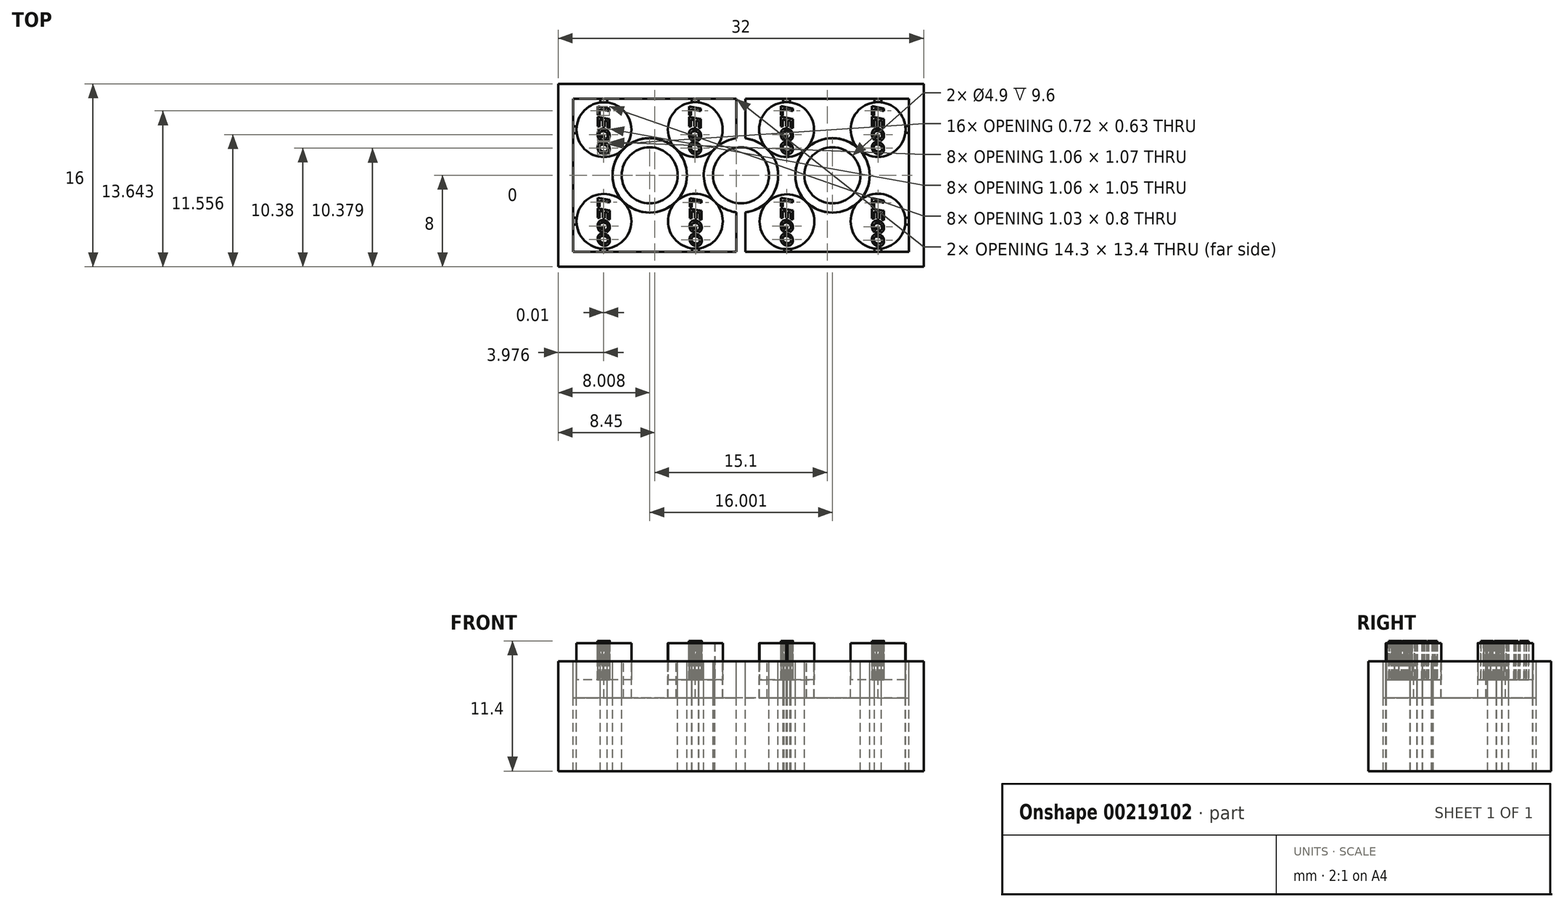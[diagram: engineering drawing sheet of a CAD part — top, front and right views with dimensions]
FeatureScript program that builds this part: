
annotation { "Feature Type Name" : "Feature", "Feature Type Description" : "" }
export const myFeature = defineFeature(function(context is Context, id is Id, definition is map)
    precondition{}
    {
        {
            var Q0;
            Q0=qCreatedBy(makeId("Top.planeOp"),FACE);
            var sketch = newSketch(context, id + "F0", { "sketchPlane" : qUnion([Q0])});
            skLineSegment(sketch, "E0.bottom", {"start": v(-16, 8) * mm, "end": v(16, 8) * mm});
            skLineSegment(sketch, "E0.top", {"start": v(-16, -8) * mm, "end": v(16, -8) * mm});
            skLineSegment(sketch, "E0.left", {"start": v(-16, 8) * mm, "end": v(-16, -8) * mm});
            skLineSegment(sketch, "E0.right", {"start": v(16, 8) * mm, "end": v(16, -8) * mm});
            skCircle(sketch, "E1", {"center": v(-12, 4) * mm, "radius": 2.4 * mm});
            skCircle(sketch, "E2", {"center": v(-4, 4) * mm, "radius": 2.4 * mm});
            skCircle(sketch, "E3", {"center": v(4, 4) * mm, "radius": 2.4 * mm});
            skCircle(sketch, "E4", {"center": v(12, 4.01) * mm, "radius": 2.4 * mm});
            skCircle(sketch, "E5", {"center": v(-12, -4.02) * mm, "radius": 2.4 * mm});
            skCircle(sketch, "E6", {"center": v(-3.99, -4.01) * mm, "radius": 2.4 * mm});
            skCircle(sketch, "E7", {"center": v(4.03, -4.05) * mm, "radius": 2.4 * mm});
            skCircle(sketch, "E8", {"center": v(12, -4.02) * mm, "radius": 2.4 * mm});
            skCircle(sketch, "E9", {"center": v(-8, 0) * mm, "radius": 3.26 * mm});
            skCircle(sketch, "E10", {"center": v(8, 0) * mm, "radius": 3.26 * mm});
            skLineSegment(sketch, "E11.0", {"start": v(-14.7, 6.7) * mm, "end": v(14.7, 6.7) * mm});
            skLineSegment(sketch, "E11.1", {"start": v(-14.7, 6.7) * mm, "end": v(-14.7, -6.7) * mm});
            skLineSegment(sketch, "E11.2", {"start": v(-14.7, -6.7) * mm, "end": v(14.7, -6.7) * mm});
            skLineSegment(sketch, "E11.3", {"start": v(14.7, 6.7) * mm, "end": v(14.7, -6.7) * mm});
            skCircle(sketch, "E12", {"center": v(0, 0) * mm, "radius": 3.26 * mm});
            skLineSegment(sketch, "E13", {"start": v(0.4, -6.7) * mm, "end": v(0.4, -3.23) * mm});
            skLineSegment(sketch, "E14", {"start": v(-0.4, -6.7) * mm, "end": v(-0.4, -3.23) * mm});
            skLineSegment(sketch, "E15.MirrorCS", {"start": v(-0.4, 6.7) * mm, "end": v(-0.4, 3.23) * mm});
            skLineSegment(sketch, "E16.MirrorCS", {"start": v(0.4, 6.7) * mm, "end": v(0.4, 3.23) * mm});
            skCircle(sketch, "E17", {"center": v(-8, 0) * mm, "radius": 2.45 * mm});
            skCircle(sketch, "E18", {"center": v(0, 0) * mm, "radius": 2.45 * mm});
            skCircle(sketch, "E19", {"center": v(8, 0) * mm, "radius": 2.45 * mm});
            skText(sketch, "E20", { "text": "LEGO", "fontName": "Arimo-BoldItalic.ttf"});
            skLineSegment(sketch, "E21", {"start": v(-12, -6.42) * mm, "end": v(-11.7, -6.42) * mm});
            skLineSegment(sketch, "E22", {"start": v(-11.7, -6.42) * mm, "end": v(-11.7, -6.7) * mm});
            skLineSegment(sketch, "E23", {"start": v(-12, -6.42) * mm, "end": v(-12.3, -6.42) * mm});
            skLineSegment(sketch, "E24", {"start": v(-12.3, -6.42) * mm, "end": v(-12.3, -6.7) * mm});
            skLineSegment(sketch, "E25", {"start": v(-14.4, -4.02) * mm, "end": v(-14.4, -3.72) * mm});
            skLineSegment(sketch, "E26", {"start": v(-14.4, -4.02) * mm, "end": v(-14.4, -4.32) * mm});
            skLineSegment(sketch, "E27", {"start": v(-14.4, -4.32) * mm, "end": v(-14.7, -4.32) * mm});
            skLineSegment(sketch, "E28", {"start": v(-14.4, -3.72) * mm, "end": v(-14.7, -3.72) * mm});
            skLineSegment(sketch, "E29", {"start": v(-14.4, 4) * mm, "end": v(-14.4, 4.3) * mm});
            skLineSegment(sketch, "E30", {"start": v(-14.4, 4) * mm, "end": v(-14.4, 3.7) * mm});
            skLineSegment(sketch, "E31", {"start": v(-14.4, 4.3) * mm, "end": v(-14.7, 4.3) * mm});
            skLineSegment(sketch, "E32", {"start": v(-14.4, 3.7) * mm, "end": v(-14.7, 3.7) * mm});
            skLineSegment(sketch, "E33", {"start": v(-12, 6.4) * mm, "end": v(-11.7, 6.4) * mm});
            skLineSegment(sketch, "E34", {"start": v(-12, 6.4) * mm, "end": v(-12.3, 6.4) * mm});
            skLineSegment(sketch, "E35", {"start": v(-11.7, 6.4) * mm, "end": v(-11.7, 6.7) * mm});
            skLineSegment(sketch, "E36", {"start": v(-12.3, 6.4) * mm, "end": v(-12.3, 6.7) * mm});
            skLineSegment(sketch, "E37", {"start": v(-4, 6.4) * mm, "end": v(-3.7, 6.4) * mm});
            skLineSegment(sketch, "E38", {"start": v(-4, 6.4) * mm, "end": v(-4.3, 6.4) * mm});
            skLineSegment(sketch, "E39", {"start": v(-4.3, 6.4) * mm, "end": v(-4.3, 6.7) * mm});
            skLineSegment(sketch, "E40", {"start": v(-3.7, 6.4) * mm, "end": v(-3.7, 6.7) * mm});
            skLineSegment(sketch, "E41", {"start": v(4.07, -6.45) * mm, "end": v(4.37, -6.45) * mm});
            skLineSegment(sketch, "E42", {"start": v(4.07, -6.45) * mm, "end": v(3.77, -6.45) * mm});
            skLineSegment(sketch, "E43", {"start": v(4.37, -6.45) * mm, "end": v(4.37, -6.7) * mm});
            skLineSegment(sketch, "E44", {"start": v(3.77, -6.45) * mm, "end": v(3.77, -6.7) * mm});
            skLineSegment(sketch, "E45", {"start": v(4, 6.4) * mm, "end": v(4.3, 6.4) * mm});
            skLineSegment(sketch, "E46", {"start": v(4, 6.4) * mm, "end": v(3.7, 6.4) * mm});
            skLineSegment(sketch, "E47", {"start": v(3.7, 6.4) * mm, "end": v(3.7, 6.7) * mm});
            skLineSegment(sketch, "E48", {"start": v(4.3, 6.4) * mm, "end": v(4.3, 6.7) * mm});
            skLineSegment(sketch, "E49", {"start": v(14.4, -4.02) * mm, "end": v(14.4, -4.32) * mm});
            skLineSegment(sketch, "E50", {"start": v(14.4, -3.72) * mm, "end": v(14.7, -3.72) * mm});
            skLineSegment(sketch, "E51", {"start": v(14.4, -4.32) * mm, "end": v(14.7, -4.32) * mm});
            skLineSegment(sketch, "E52", {"start": v(12, 6.41) * mm, "end": v(12.3, 6.41) * mm});
            skLineSegment(sketch, "E53", {"start": v(12, 6.41) * mm, "end": v(11.7, 6.41) * mm});
            skLineSegment(sketch, "E54", {"start": v(11.7, 6.41) * mm, "end": v(11.7, 6.7) * mm});
            skLineSegment(sketch, "E55", {"start": v(12.3, 6.41) * mm, "end": v(12.3, 6.7) * mm});
            skLineSegment(sketch, "E56", {"start": v(14.4, 4.01) * mm, "end": v(14.4, 4.31) * mm});
            skLineSegment(sketch, "E57", {"start": v(14.4, 4.01) * mm, "end": v(14.4, 3.71) * mm});
            skLineSegment(sketch, "E58", {"start": v(14.4, 3.71) * mm, "end": v(14.7, 3.71) * mm});
            skLineSegment(sketch, "E59", {"start": v(14.4, 4.31) * mm, "end": v(14.7, 4.31) * mm});
            skText(sketch, "E60", { "text": "LEGO", "fontName": "Arimo-BoldItalic.ttf"});
            skText(sketch, "E61", { "text": "LEGO", "fontName": "Arimo-BoldItalic.ttf"});
            skText(sketch, "E62", { "text": "LEGO", "fontName": "Arimo-BoldItalic.ttf"});
            skText(sketch, "E63", { "text": "LEGO", "fontName": "Arimo-BoldItalic.ttf"});
            skText(sketch, "E64", { "text": "LEGO", "fontName": "Arimo-BoldItalic.ttf"});
            skText(sketch, "E65", { "text": "LEGO", "fontName": "Arimo-BoldItalic.ttf"});
            skText(sketch, "E66", { "text": "LEGO", "fontName": "Arimo-BoldItalic.ttf"});
            skLineSegment(sketch, "E67.bottom", {"start": v(14.7, 6.7) * mm, "end": v(-14.7, 6.7) * mm});
            skLineSegment(sketch, "E67.top", {"start": v(14.7, -6.7) * mm, "end": v(-14.7, -6.7) * mm});
            skLineSegment(sketch, "E68", {"start": v(14.4, -3.72) * mm, "end": v(14.4, -4.02) * mm});
            skLineSegment(sketch, "E69", {"start": v(12, -6.42) * mm, "end": v(12.3, -6.42) * mm});
            skLineSegment(sketch, "E70", {"start": v(12, -6.42) * mm, "end": v(11.7, -6.42) * mm});
            skLineSegment(sketch, "E71", {"start": v(11.7, -6.42) * mm, "end": v(11.7, -6.7) * mm});
            skLineSegment(sketch, "E72", {"start": v(12.3, -6.42) * mm, "end": v(12.3, -6.7) * mm});
            skLineSegment(sketch, "E73", {"start": v(-3.99, -6.41) * mm, "end": v(-3.69, -6.41) * mm});
            skLineSegment(sketch, "E74", {"start": v(-3.99, -6.41) * mm, "end": v(-4.29, -6.41) * mm});
            skLineSegment(sketch, "E75", {"start": v(-4.29, -6.41) * mm, "end": v(-4.29, -6.7) * mm});
            skLineSegment(sketch, "E76", {"start": v(-3.69, -6.41) * mm, "end": v(-3.69, -6.7) * mm});
            skLineSegment(sketch, "E77", {"start": v(2.3, 2.3) * mm, "end": v(2.3, 2.3) * mm});
            skLineSegment(sketch, "E78", {"start": v(5.7, 2.33) * mm, "end": v(5.72, 2.32) * mm});
            skLineSegment(sketch, "E79", {"start": v(5.74, -2.34) * mm, "end": v(5.72, -2.35) * mm});
            skLineSegment(sketch, "E80", {"start": v(10.29, 2.34) * mm, "end": v(10.28, 2.33) * mm});
            skLineSegment(sketch, "E81", {"start": v(-10.3, -2.34) * mm, "end": v(-10.28, -2.32) * mm});
            skLineSegment(sketch, "E82", {"start": v(-5.7, 2.3) * mm, "end": v(-5.7, 2.3) * mm});
            const initialGuessF0  = {"E20": [-0.00454, 0.00607, 0, -1, 0.00108], "E60": [-0.01254, 0.00607, 0, -1, 0.00108], "E61": [0.0035, 0.00608, 0, -1, 0.00108], "E62": [0.01148, 0.00608, 0, -1, 0.00108], "E63": [-0.00448, -0.00196, 0, -1, 0.00108], "E64": [-0.01253, -0.00193, 0, -1, 0.00108], "E65": [0.0035, -0.00193, 0, -1, 0.00108], "E66": [0.01148, -0.00198, 0, -1, 0.00108]};
            skSetInitialGuess(sketch, initialGuessF0);
            skSolve(sketch);
        }
        {
            var Q0;
            Q0=makeQuery(id+"F0.imprint","IMPRINT",FACE,{"disambiguationData":[TD([[makeQuery(id+"F0.imprint","IMPRINT",EDGE,{"derivedFrom":sQuery(id+"F0.wireOp",EDGE,"E0.bottom")}),-1.0]])]});
            var Q1;
            Q1=makeQuery(id+"F0.imprint","IMPRINT",FACE,{"disambiguationData":[TD([[makeQuery(id+"F0.imprint","IMPRINT",EDGE,{"derivedFrom":sQuery(id+"F0.wireOp",EDGE,"E9")}),1.0]])]});
            var Q2;
            Q2=makeQuery(id+"F0.imprint","IMPRINT",FACE,{"disambiguationData":[TD([[makeQuery(id+"F0.imprint","IMPRINT",EDGE,{"derivedFrom":sQuery(id+"F0.wireOp",EDGE,"E18")}),-1.0]])]});
            var Q3;
            {var subQ0=sQuery(id+"F0.wireOp",EDGE,"E15.MirrorCS");Q3=makeQuery(id+"F0.imprint","IMPRINT",FACE,{"disambiguationData":[TD([[makeQuery(id+"F0.imprint","IMPRINT",EDGE,{"derivedFrom":subQ0}),1.0]])]});}
            var Q4;
            {var subQ0=sQuery(id+"F0.wireOp",EDGE,"E13");Q4=makeQuery(id+"F0.imprint","IMPRINT",FACE,{"disambiguationData":[TD([[makeQuery(id+"F0.imprint","IMPRINT",EDGE,{"derivedFrom":subQ0}),1.0]])]});}
            var Q5;
            Q5=makeQuery(id+"F0.imprint","IMPRINT",FACE,{"disambiguationData":[TD([[makeQuery(id+"F0.imprint","IMPRINT",EDGE,{"derivedFrom":sQuery(id+"F0.wireOp",EDGE,"E10")}),1.0]])]});
            extrude(context, id + "F1", {"entities" : qUnion([Q0, Q1, Q2, Q3, Q4, Q5]), "oppositeDirection" : true, "depth" : 9.6 * mm});
        }
        {
            var Q0;
            Q0=makeQuery(id+"F0.imprint","IMPRINT",FACE,{"disambiguationData":[TD([[makeQuery(id+"F0.imprint","IMPRINT",EDGE,{"derivedFrom":sQuery(id+"F0.wireOp",EDGE,"E65.sketch_text.stroke-0")}),1.0]])]});
            var Q1;
            Q1=makeQuery(id+"F0.imprint","IMPRINT",FACE,{"disambiguationData":[TD([[makeQuery(id+"F0.imprint","IMPRINT",EDGE,{"derivedFrom":sQuery(id+"F0.wireOp",EDGE,"E65.sketch_text.stroke-53")}),1.0]])]});
            var Q2;
            Q2=makeQuery(id+"F0.imprint","IMPRINT",FACE,{"disambiguationData":[TD([[makeQuery(id+"F0.imprint","IMPRINT",EDGE,{"derivedFrom":sQuery(id+"F0.wireOp",EDGE,"E66.sketch_text.stroke-53")}),1.0]])]});
            var Q3;
            Q3=makeQuery(id+"F0.imprint","IMPRINT",FACE,{"disambiguationData":[TD([[makeQuery(id+"F0.imprint","IMPRINT",EDGE,{"derivedFrom":sQuery(id+"F0.wireOp",EDGE,"E66.sketch_text.stroke-0")}),1.0]])]});
            var Q4;
            Q4=makeQuery(id+"F0.imprint","IMPRINT",FACE,{"disambiguationData":[TD([[makeQuery(id+"F0.imprint","IMPRINT",EDGE,{"derivedFrom":sQuery(id+"F0.wireOp",EDGE,"E63.sketch_text.stroke-0")}),1.0]])]});
            var Q5;
            Q5=makeQuery(id+"F0.imprint","IMPRINT",FACE,{"disambiguationData":[TD([[makeQuery(id+"F0.imprint","IMPRINT",EDGE,{"derivedFrom":sQuery(id+"F0.wireOp",EDGE,"E63.sketch_text.stroke-53")}),1.0]])]});
            var Q6;
            Q6=makeQuery(id+"F0.imprint","IMPRINT",FACE,{"disambiguationData":[TD([[makeQuery(id+"F0.imprint","IMPRINT",EDGE,{"derivedFrom":sQuery(id+"F0.wireOp",EDGE,"E64.sketch_text.stroke-0")}),1.0]])]});
            var Q7;
            Q7=makeQuery(id+"F0.imprint","IMPRINT",FACE,{"disambiguationData":[TD([[makeQuery(id+"F0.imprint","IMPRINT",EDGE,{"derivedFrom":sQuery(id+"F0.wireOp",EDGE,"E64.sketch_text.stroke-53")}),1.0]])]});
            var Q8;
            Q8=makeQuery(id+"F0.imprint","IMPRINT",FACE,{"disambiguationData":[TD([[makeQuery(id+"F0.imprint","IMPRINT",EDGE,{"derivedFrom":sQuery(id+"F0.wireOp",EDGE,"E60.sketch_text.stroke-0")}),1.0]])]});
            var Q9;
            Q9=makeQuery(id+"F0.imprint","IMPRINT",FACE,{"disambiguationData":[TD([[makeQuery(id+"F0.imprint","IMPRINT",EDGE,{"derivedFrom":sQuery(id+"F0.wireOp",EDGE,"E60.sketch_text.stroke-53")}),1.0]])]});
            var Q10;
            Q10=makeQuery(id+"F0.imprint","IMPRINT",FACE,{"disambiguationData":[TD([[makeQuery(id+"F0.imprint","IMPRINT",EDGE,{"derivedFrom":sQuery(id+"F0.wireOp",EDGE,"E20.sketch_text.stroke-53")}),1.0]])]});
            var Q11;
            Q11=makeQuery(id+"F0.imprint","IMPRINT",FACE,{"disambiguationData":[TD([[makeQuery(id+"F0.imprint","IMPRINT",EDGE,{"derivedFrom":sQuery(id+"F0.wireOp",EDGE,"E2")}),1.0]])]});
            var Q12;
            Q12=makeQuery(id+"F0.imprint","IMPRINT",FACE,{"disambiguationData":[TD([[makeQuery(id+"F0.imprint","IMPRINT",EDGE,{"derivedFrom":sQuery(id+"F0.wireOp",EDGE,"E61.sketch_text.stroke-53")}),1.0]])]});
            var Q13;
            Q13=makeQuery(id+"F0.imprint","IMPRINT",FACE,{"disambiguationData":[TD([[makeQuery(id+"F0.imprint","IMPRINT",EDGE,{"derivedFrom":sQuery(id+"F0.wireOp",EDGE,"E3")}),1.0]])]});
            var Q14;
            Q14=makeQuery(id+"F0.imprint","IMPRINT",FACE,{"disambiguationData":[TD([[makeQuery(id+"F0.imprint","IMPRINT",EDGE,{"derivedFrom":sQuery(id+"F0.wireOp",EDGE,"E62.sketch_text.stroke-53")}),1.0]])]});
            var Q15;
            Q15=makeQuery(id+"F0.imprint","IMPRINT",FACE,{"disambiguationData":[TD([[makeQuery(id+"F0.imprint","IMPRINT",EDGE,{"derivedFrom":sQuery(id+"F0.wireOp",EDGE,"E62.sketch_text.stroke-0")}),1.0]])]});
            extrude(context, id + "F2", {"entities" : qUnion([Q0, Q1, Q2, Q3, Q4, Q5, Q6, Q7, Q8, Q9, Q10, Q11, Q12, Q13, Q14, Q15]), "endBound" : BoundingType.SYMMETRIC, "depth" : 3.2 * mm});
        }
        {
            var Q0;
            Q0=makeQuery(id+"F0.imprint","IMPRINT",FACE,{"disambiguationData":[TD([[makeQuery(id+"F0.imprint","IMPRINT",EDGE,{"derivedFrom":sQuery(id+"F0.wireOp",EDGE,"E20.sketch_text.stroke-42")}),-1.0]])]});
            var Q1;
            Q1=makeQuery(id+"F0.imprint","IMPRINT",FACE,{"disambiguationData":[TD([[makeQuery(id+"F0.imprint","IMPRINT",EDGE,{"derivedFrom":sQuery(id+"F0.wireOp",EDGE,"E20.sketch_text.stroke-18")}),-1.0]])]});
            var Q2;
            Q2=makeQuery(id+"F0.imprint","IMPRINT",FACE,{"disambiguationData":[TD([[makeQuery(id+"F0.imprint","IMPRINT",EDGE,{"derivedFrom":sQuery(id+"F0.wireOp",EDGE,"E20.sketch_text.stroke-6")}),-1.0]])]});
            var Q3;
            Q3=makeQuery(id+"F0.imprint","IMPRINT",FACE,{"disambiguationData":[TD([[makeQuery(id+"F0.imprint","IMPRINT",EDGE,{"derivedFrom":sQuery(id+"F0.wireOp",EDGE,"E20.sketch_text.stroke-0")}),-1.0]])]});
            var Q4;
            Q4=makeQuery(id+"F0.imprint","IMPRINT",FACE,{"disambiguationData":[TD([[makeQuery(id+"F0.imprint","IMPRINT",EDGE,{"derivedFrom":sQuery(id+"F0.wireOp",EDGE,"E60.sketch_text.stroke-0")}),-1.0]])]});
            var Q5;
            Q5=makeQuery(id+"F0.imprint","IMPRINT",FACE,{"disambiguationData":[TD([[makeQuery(id+"F0.imprint","IMPRINT",EDGE,{"derivedFrom":sQuery(id+"F0.wireOp",EDGE,"E60.sketch_text.stroke-6")}),-1.0]])]});
            var Q6;
            Q6=makeQuery(id+"F0.imprint","IMPRINT",FACE,{"disambiguationData":[TD([[makeQuery(id+"F0.imprint","IMPRINT",EDGE,{"derivedFrom":sQuery(id+"F0.wireOp",EDGE,"E60.sketch_text.stroke-18")}),-1.0]])]});
            var Q7;
            Q7=makeQuery(id+"F0.imprint","IMPRINT",FACE,{"disambiguationData":[TD([[makeQuery(id+"F0.imprint","IMPRINT",EDGE,{"derivedFrom":sQuery(id+"F0.wireOp",EDGE,"E60.sketch_text.stroke-42")}),-1.0]])]});
            var Q8;
            Q8=makeQuery(id+"F0.imprint","IMPRINT",FACE,{"disambiguationData":[TD([[makeQuery(id+"F0.imprint","IMPRINT",EDGE,{"derivedFrom":sQuery(id+"F0.wireOp",EDGE,"E64.sketch_text.stroke-0")}),-1.0]])]});
            var Q9;
            Q9=makeQuery(id+"F0.imprint","IMPRINT",FACE,{"disambiguationData":[TD([[makeQuery(id+"F0.imprint","IMPRINT",EDGE,{"derivedFrom":sQuery(id+"F0.wireOp",EDGE,"E64.sketch_text.stroke-6")}),-1.0]])]});
            var Q10;
            Q10=makeQuery(id+"F0.imprint","IMPRINT",FACE,{"disambiguationData":[TD([[makeQuery(id+"F0.imprint","IMPRINT",EDGE,{"derivedFrom":sQuery(id+"F0.wireOp",EDGE,"E64.sketch_text.stroke-18")}),-1.0]])]});
            var Q11;
            Q11=makeQuery(id+"F0.imprint","IMPRINT",FACE,{"disambiguationData":[TD([[makeQuery(id+"F0.imprint","IMPRINT",EDGE,{"derivedFrom":sQuery(id+"F0.wireOp",EDGE,"E64.sketch_text.stroke-42")}),-1.0]])]});
            var Q12;
            Q12=makeQuery(id+"F0.imprint","IMPRINT",FACE,{"disambiguationData":[TD([[makeQuery(id+"F0.imprint","IMPRINT",EDGE,{"derivedFrom":sQuery(id+"F0.wireOp",EDGE,"E63.sketch_text.stroke-42")}),-1.0]])]});
            var Q13;
            Q13=makeQuery(id+"F0.imprint","IMPRINT",FACE,{"disambiguationData":[TD([[makeQuery(id+"F0.imprint","IMPRINT",EDGE,{"derivedFrom":sQuery(id+"F0.wireOp",EDGE,"E63.sketch_text.stroke-18")}),-1.0]])]});
            var Q14;
            Q14=makeQuery(id+"F0.imprint","IMPRINT",FACE,{"disambiguationData":[TD([[makeQuery(id+"F0.imprint","IMPRINT",EDGE,{"derivedFrom":sQuery(id+"F0.wireOp",EDGE,"E63.sketch_text.stroke-6")}),-1.0]])]});
            var Q15;
            Q15=makeQuery(id+"F0.imprint","IMPRINT",FACE,{"disambiguationData":[TD([[makeQuery(id+"F0.imprint","IMPRINT",EDGE,{"derivedFrom":sQuery(id+"F0.wireOp",EDGE,"E63.sketch_text.stroke-0")}),-1.0]])]});
            var Q16;
            Q16=makeQuery(id+"F0.imprint","IMPRINT",FACE,{"disambiguationData":[TD([[makeQuery(id+"F0.imprint","IMPRINT",EDGE,{"derivedFrom":sQuery(id+"F0.wireOp",EDGE,"E65.sketch_text.stroke-18")}),-1.0]])]});
            var Q17;
            Q17=makeQuery(id+"F0.imprint","IMPRINT",FACE,{"disambiguationData":[TD([[makeQuery(id+"F0.imprint","IMPRINT",EDGE,{"derivedFrom":sQuery(id+"F0.wireOp",EDGE,"E65.sketch_text.stroke-42")}),-1.0]])]});
            var Q18;
            Q18=makeQuery(id+"F0.imprint","IMPRINT",FACE,{"disambiguationData":[TD([[makeQuery(id+"F0.imprint","IMPRINT",EDGE,{"derivedFrom":sQuery(id+"F0.wireOp",EDGE,"E65.sketch_text.stroke-6")}),-1.0]])]});
            var Q19;
            Q19=makeQuery(id+"F0.imprint","IMPRINT",FACE,{"disambiguationData":[TD([[makeQuery(id+"F0.imprint","IMPRINT",EDGE,{"derivedFrom":sQuery(id+"F0.wireOp",EDGE,"E65.sketch_text.stroke-0")}),-1.0]])]});
            var Q20;
            Q20=makeQuery(id+"F0.imprint","IMPRINT",FACE,{"disambiguationData":[TD([[makeQuery(id+"F0.imprint","IMPRINT",EDGE,{"derivedFrom":sQuery(id+"F0.wireOp",EDGE,"E61.sketch_text.stroke-42")}),-1.0]])]});
            var Q21;
            Q21=makeQuery(id+"F0.imprint","IMPRINT",FACE,{"disambiguationData":[TD([[makeQuery(id+"F0.imprint","IMPRINT",EDGE,{"derivedFrom":sQuery(id+"F0.wireOp",EDGE,"E61.sketch_text.stroke-18")}),-1.0]])]});
            var Q22;
            Q22=makeQuery(id+"F0.imprint","IMPRINT",FACE,{"disambiguationData":[TD([[makeQuery(id+"F0.imprint","IMPRINT",EDGE,{"derivedFrom":sQuery(id+"F0.wireOp",EDGE,"E61.sketch_text.stroke-6")}),-1.0]])]});
            var Q23;
            Q23=makeQuery(id+"F0.imprint","IMPRINT",FACE,{"disambiguationData":[TD([[makeQuery(id+"F0.imprint","IMPRINT",EDGE,{"derivedFrom":sQuery(id+"F0.wireOp",EDGE,"E61.sketch_text.stroke-0")}),-1.0]])]});
            var Q24;
            Q24=makeQuery(id+"F0.imprint","IMPRINT",FACE,{"disambiguationData":[TD([[makeQuery(id+"F0.imprint","IMPRINT",EDGE,{"derivedFrom":sQuery(id+"F0.wireOp",EDGE,"E62.sketch_text.stroke-0")}),-1.0]])]});
            var Q25;
            Q25=makeQuery(id+"F0.imprint","IMPRINT",FACE,{"disambiguationData":[TD([[makeQuery(id+"F0.imprint","IMPRINT",EDGE,{"derivedFrom":sQuery(id+"F0.wireOp",EDGE,"E62.sketch_text.stroke-6")}),-1.0]])]});
            var Q26;
            Q26=makeQuery(id+"F0.imprint","IMPRINT",FACE,{"disambiguationData":[TD([[makeQuery(id+"F0.imprint","IMPRINT",EDGE,{"derivedFrom":sQuery(id+"F0.wireOp",EDGE,"E62.sketch_text.stroke-18")}),-1.0]])]});
            var Q27;
            Q27=makeQuery(id+"F0.imprint","IMPRINT",FACE,{"disambiguationData":[TD([[makeQuery(id+"F0.imprint","IMPRINT",EDGE,{"derivedFrom":sQuery(id+"F0.wireOp",EDGE,"E62.sketch_text.stroke-42")}),-1.0]])]});
            var Q28;
            Q28=makeQuery(id+"F0.imprint","IMPRINT",FACE,{"disambiguationData":[TD([[makeQuery(id+"F0.imprint","IMPRINT",EDGE,{"derivedFrom":sQuery(id+"F0.wireOp",EDGE,"E66.sketch_text.stroke-0")}),-1.0]])]});
            var Q29;
            Q29=makeQuery(id+"F0.imprint","IMPRINT",FACE,{"disambiguationData":[TD([[makeQuery(id+"F0.imprint","IMPRINT",EDGE,{"derivedFrom":sQuery(id+"F0.wireOp",EDGE,"E66.sketch_text.stroke-6")}),-1.0]])]});
            var Q30;
            Q30=makeQuery(id+"F0.imprint","IMPRINT",FACE,{"disambiguationData":[TD([[makeQuery(id+"F0.imprint","IMPRINT",EDGE,{"derivedFrom":sQuery(id+"F0.wireOp",EDGE,"E66.sketch_text.stroke-18")}),-1.0]])]});
            var Q31;
            Q31=makeQuery(id+"F0.imprint","IMPRINT",FACE,{"disambiguationData":[TD([[makeQuery(id+"F0.imprint","IMPRINT",EDGE,{"derivedFrom":sQuery(id+"F0.wireOp",EDGE,"E66.sketch_text.stroke-42")}),-1.0]])]});
            extrude(context, id + "F3", {"entities" : qUnion([Q0, Q1, Q2, Q3, Q4, Q5, Q6, Q7, Q8, Q9, Q10, Q11, Q12, Q13, Q14, Q15, Q16, Q17, Q18, Q19, Q20, Q21, Q22, Q23, Q24, Q25, Q26, Q27, Q28, Q29, Q30, Q31]), "depth" : 1.8 * mm});
        }
        {
            var Q0;
            Q0=makeQuery(id+"F0.imprint","IMPRINT",FACE,{"disambiguationData":[TD([[makeQuery(id+"F0.imprint","IMPRINT",EDGE,{"derivedFrom":sQuery(id+"F0.wireOp",EDGE,"E18")}),1.0]])]});
            var Q1;
            Q1=makeQuery(id+"F0.imprint","IMPRINT",FACE,{"disambiguationData":[TD([[makeQuery(id+"F0.imprint","IMPRINT",EDGE,{"derivedFrom":sQuery(id+"F0.wireOp",EDGE,"E17")}),1.0]])]});
            var Q2;
            Q2=makeQuery(id+"F0.imprint","IMPRINT",FACE,{"disambiguationData":[TD([[makeQuery(id+"F0.imprint","IMPRINT",EDGE,{"derivedFrom":sQuery(id+"F0.wireOp",EDGE,"E19")}),1.0]])]});
            extrude(context, id + "F4", {"entities" : qUnion([Q0, Q1, Q2]), "oppositeDirection" : true, "depth" : 3.2 * mm});
        }
        {
            var Q0;
            {var subQ0=sQuery(id+"F0.wireOp",EDGE,"E45");Q0=makeQuery(id+"F0.imprint","IMPRINT",FACE,{"disambiguationData":[TD([[makeQuery(id+"F0.imprint","IMPRINT",EDGE,{"derivedFrom":subQ0}),-1.0]])]});}
            var Q1;
            {var subQ1=sQuery(id+"F0.wireOp",EDGE,"E16.MirrorCS");Q1=makeQuery(id+"F0.imprint","IMPRINT",FACE,{"disambiguationData":[TD([[makeQuery(id+"F0.imprint","IMPRINT",EDGE,{"derivedFrom":subQ1}),1.0]])]});}
            var Q2;
            {var subQ0=sQuery(id+"F0.wireOp",EDGE,"E52");Q2=makeQuery(id+"F0.imprint","IMPRINT",FACE,{"disambiguationData":[TD([[makeQuery(id+"F0.imprint","IMPRINT",EDGE,{"derivedFrom":subQ0}),-1.0]])]});}
            var Q3;
            {var subQ5=sQuery(id+"F0.wireOp",EDGE,"E41");Q3=makeQuery(id+"F0.imprint","IMPRINT",FACE,{"disambiguationData":[TD([[makeQuery(id+"F0.imprint","IMPRINT",EDGE,{"derivedFrom":subQ5}),1.0]])]});}
            var Q4;
            {var subQ5=sQuery(id+"F0.wireOp",EDGE,"E49");Q4=makeQuery(id+"F0.imprint","IMPRINT",FACE,{"disambiguationData":[TD([[makeQuery(id+"F0.imprint","IMPRINT",EDGE,{"derivedFrom":subQ5}),-1.0]])]});}
            extrude(context, id + "F5", {"entities" : qUnion([Q0, Q1, Q2, Q3, Q4]), "oppositeDirection" : true, "depth" : 3.2 * mm});
        }
        {
            var Q0;
            {var subQ2=sQuery(id+"F0.wireOp",EDGE,"E13");Q0=makeQuery(id+"F0.imprint","IMPRINT",FACE,{"disambiguationData":[TD([[makeQuery(id+"F0.imprint","IMPRINT",EDGE,{"derivedFrom":subQ2}),-1.0]])]});}
            extrude(context, id + "F6", {"entities" : qUnion([Q0]), "oppositeDirection" : true, "depth" : 3.2 * mm});
        }
        {
            var Q0;
            {var subQ1=sQuery(id+"F0.wireOp",EDGE,"E14");Q0=makeQuery(id+"F0.imprint","IMPRINT",FACE,{"disambiguationData":[TD([[makeQuery(id+"F0.imprint","IMPRINT",EDGE,{"derivedFrom":subQ1}),1.0]])]});}
            var Q1;
            {var subQ1=sQuery(id+"F0.wireOp",EDGE,"E29");Q1=makeQuery(id+"F0.imprint","IMPRINT",FACE,{"disambiguationData":[TD([[makeQuery(id+"F0.imprint","IMPRINT",EDGE,{"derivedFrom":subQ1}),-1.0]])]});}
            var Q2;
            {var subQ2=sQuery(id+"F0.wireOp",EDGE,"E23");Q2=makeQuery(id+"F0.imprint","IMPRINT",FACE,{"disambiguationData":[TD([[makeQuery(id+"F0.imprint","IMPRINT",EDGE,{"derivedFrom":subQ2}),-1.0]])]});}
            var Q3;
            {var subQ3=sQuery(id+"F0.wireOp",EDGE,"E15.MirrorCS");Q3=makeQuery(id+"F0.imprint","IMPRINT",FACE,{"disambiguationData":[TD([[makeQuery(id+"F0.imprint","IMPRINT",EDGE,{"derivedFrom":subQ3}),-1.0]])]});}
            extrude(context, id + "F7", {"entities" : qUnion([Q0, Q1, Q2, Q3]), "oppositeDirection" : true, "depth" : 3.2 * mm});
        }
        {
            var Q0;
            {var subQ9=sQuery(id+"F0.wireOp",EDGE,"E25");Q0=makeQuery(id+"F0.imprint","IMPRINT",FACE,{"disambiguationData":[TD([[makeQuery(id+"F0.imprint","IMPRINT",EDGE,{"derivedFrom":subQ9}),-1.0]])]});}
            extrude(context, id + "F8", {"entities" : qUnion([Q0]), "oppositeDirection" : true, "depth" : 3.2 * mm});
        }
        {
            var Q0;
            Q0=makeQuery(id+"F0.imprint","IMPRINT",FACE,{"disambiguationData":[TD([[makeQuery(id+"F0.imprint","IMPRINT",EDGE,{"derivedFrom":sQuery(id+"F0.wireOp",EDGE,"E52")}),1.0]])]});
            var Q1;
            Q1=makeQuery(id+"F0.imprint","IMPRINT",FACE,{"disambiguationData":[TD([[makeQuery(id+"F0.imprint","IMPRINT",EDGE,{"derivedFrom":sQuery(id+"F0.wireOp",EDGE,"E56")}),-1.0]])]});
            var Q2;
            {var subQ3=sQuery(id+"F0.wireOp",EDGE,"E49");Q2=makeQuery(id+"F0.imprint","IMPRINT",FACE,{"disambiguationData":[TD([[makeQuery(id+"F0.imprint","IMPRINT",EDGE,{"derivedFrom":subQ3}),1.0]])]});}
            var Q3;
            Q3=makeQuery(id+"F0.imprint","IMPRINT",FACE,{"disambiguationData":[TD([[makeQuery(id+"F0.imprint","IMPRINT",EDGE,{"derivedFrom":sQuery(id+"F0.wireOp",EDGE,"E69")}),-1.0]])]});
            var Q4;
            {var subQ6=sQuery(id+"F0.wireOp",EDGE,"E41");Q4=makeQuery(id+"F0.imprint","IMPRINT",FACE,{"disambiguationData":[TD([[makeQuery(id+"F0.imprint","IMPRINT",EDGE,{"derivedFrom":subQ6}),-1.0]])]});}
            var Q5;
            Q5=makeQuery(id+"F0.imprint","IMPRINT",FACE,{"disambiguationData":[TD([[makeQuery(id+"F0.imprint","IMPRINT",EDGE,{"derivedFrom":sQuery(id+"F0.wireOp",EDGE,"E45")}),1.0]])]});
            var Q6;
            Q6=makeQuery(id+"F0.imprint","IMPRINT",FACE,{"disambiguationData":[TD([[makeQuery(id+"F0.imprint","IMPRINT",EDGE,{"derivedFrom":sQuery(id+"F0.wireOp",EDGE,"E37")}),1.0]])]});
            var Q7;
            Q7=makeQuery(id+"F0.imprint","IMPRINT",FACE,{"disambiguationData":[TD([[makeQuery(id+"F0.imprint","IMPRINT",EDGE,{"derivedFrom":sQuery(id+"F0.wireOp",EDGE,"E73")}),-1.0]])]});
            var Q8;
            Q8=makeQuery(id+"F0.imprint","IMPRINT",FACE,{"disambiguationData":[TD([[makeQuery(id+"F0.imprint","IMPRINT",EDGE,{"derivedFrom":sQuery(id+"F0.wireOp",EDGE,"E21")}),-1.0]])]});
            var Q9;
            Q9=makeQuery(id+"F0.imprint","IMPRINT",FACE,{"disambiguationData":[TD([[makeQuery(id+"F0.imprint","IMPRINT",EDGE,{"derivedFrom":sQuery(id+"F0.wireOp",EDGE,"E25")}),1.0]])]});
            var Q10;
            Q10=makeQuery(id+"F0.imprint","IMPRINT",FACE,{"disambiguationData":[TD([[makeQuery(id+"F0.imprint","IMPRINT",EDGE,{"derivedFrom":sQuery(id+"F0.wireOp",EDGE,"E29")}),1.0]])]});
            var Q11;
            Q11=makeQuery(id+"F0.imprint","IMPRINT",FACE,{"disambiguationData":[TD([[makeQuery(id+"F0.imprint","IMPRINT",EDGE,{"derivedFrom":sQuery(id+"F0.wireOp",EDGE,"E33")}),1.0]])]});
            extrude(context, id + "F9", {"entities" : qUnion([Q0, Q1, Q2, Q3, Q4, Q5, Q6, Q7, Q8, Q9, Q10, Q11]), "oppositeDirection" : true, "depth" : 9.6 * mm});
        }
        {
            var Q0;
            Q0=makeQuery(id+"F0.imprint","IMPRINT",FACE,{"disambiguationData":[TD([[makeQuery(id+"F0.imprint","IMPRINT",EDGE,{"derivedFrom":sQuery(id+"F0.wireOp",EDGE,"E60.sketch_text.stroke-42")}),-1.0]])]});
            var Q1;
            Q1=makeQuery(id+"F0.imprint","IMPRINT",FACE,{"disambiguationData":[TD([[makeQuery(id+"F0.imprint","IMPRINT",EDGE,{"derivedFrom":sQuery(id+"F0.wireOp",EDGE,"E60.sketch_text.stroke-18")}),-1.0]])]});
            var Q2;
            Q2=makeQuery(id+"F0.imprint","IMPRINT",FACE,{"disambiguationData":[TD([[makeQuery(id+"F0.imprint","IMPRINT",EDGE,{"derivedFrom":sQuery(id+"F0.wireOp",EDGE,"E60.sketch_text.stroke-6")}),-1.0]])]});
            var Q3;
            Q3=makeQuery(id+"F0.imprint","IMPRINT",FACE,{"disambiguationData":[TD([[makeQuery(id+"F0.imprint","IMPRINT",EDGE,{"derivedFrom":sQuery(id+"F0.wireOp",EDGE,"E60.sketch_text.stroke-0")}),-1.0]])]});
            var Q4;
            Q4=makeQuery(id+"F0.imprint","IMPRINT",FACE,{"disambiguationData":[TD([[makeQuery(id+"F0.imprint","IMPRINT",EDGE,{"derivedFrom":sQuery(id+"F0.wireOp",EDGE,"E20.sketch_text.stroke-42")}),-1.0]])]});
            var Q5;
            Q5=makeQuery(id+"F0.imprint","IMPRINT",FACE,{"disambiguationData":[TD([[makeQuery(id+"F0.imprint","IMPRINT",EDGE,{"derivedFrom":sQuery(id+"F0.wireOp",EDGE,"E20.sketch_text.stroke-18")}),-1.0]])]});
            var Q6;
            Q6=makeQuery(id+"F0.imprint","IMPRINT",FACE,{"disambiguationData":[TD([[makeQuery(id+"F0.imprint","IMPRINT",EDGE,{"derivedFrom":sQuery(id+"F0.wireOp",EDGE,"E20.sketch_text.stroke-6")}),-1.0]])]});
            var Q7;
            Q7=makeQuery(id+"F0.imprint","IMPRINT",FACE,{"disambiguationData":[TD([[makeQuery(id+"F0.imprint","IMPRINT",EDGE,{"derivedFrom":sQuery(id+"F0.wireOp",EDGE,"E20.sketch_text.stroke-0")}),-1.0]])]});
            var Q8;
            Q8=makeQuery(id+"F0.imprint","IMPRINT",FACE,{"disambiguationData":[TD([[makeQuery(id+"F0.imprint","IMPRINT",EDGE,{"derivedFrom":sQuery(id+"F0.wireOp",EDGE,"E61.sketch_text.stroke-42")}),-1.0]])]});
            var Q9;
            Q9=makeQuery(id+"F0.imprint","IMPRINT",FACE,{"disambiguationData":[TD([[makeQuery(id+"F0.imprint","IMPRINT",EDGE,{"derivedFrom":sQuery(id+"F0.wireOp",EDGE,"E61.sketch_text.stroke-18")}),-1.0]])]});
            var Q10;
            Q10=makeQuery(id+"F0.imprint","IMPRINT",FACE,{"disambiguationData":[TD([[makeQuery(id+"F0.imprint","IMPRINT",EDGE,{"derivedFrom":sQuery(id+"F0.wireOp",EDGE,"E61.sketch_text.stroke-6")}),-1.0]])]});
            var Q11;
            Q11=makeQuery(id+"F0.imprint","IMPRINT",FACE,{"disambiguationData":[TD([[makeQuery(id+"F0.imprint","IMPRINT",EDGE,{"derivedFrom":sQuery(id+"F0.wireOp",EDGE,"E61.sketch_text.stroke-0")}),-1.0]])]});
            var Q12;
            Q12=makeQuery(id+"F0.imprint","IMPRINT",FACE,{"disambiguationData":[TD([[makeQuery(id+"F0.imprint","IMPRINT",EDGE,{"derivedFrom":sQuery(id+"F0.wireOp",EDGE,"E62.sketch_text.stroke-18")}),-1.0]])]});
            var Q13;
            Q13=makeQuery(id+"F0.imprint","IMPRINT",FACE,{"disambiguationData":[TD([[makeQuery(id+"F0.imprint","IMPRINT",EDGE,{"derivedFrom":sQuery(id+"F0.wireOp",EDGE,"E62.sketch_text.stroke-42")}),-1.0]])]});
            var Q14;
            Q14=makeQuery(id+"F0.imprint","IMPRINT",FACE,{"disambiguationData":[TD([[makeQuery(id+"F0.imprint","IMPRINT",EDGE,{"derivedFrom":sQuery(id+"F0.wireOp",EDGE,"E62.sketch_text.stroke-6")}),-1.0]])]});
            var Q15;
            Q15=makeQuery(id+"F0.imprint","IMPRINT",FACE,{"disambiguationData":[TD([[makeQuery(id+"F0.imprint","IMPRINT",EDGE,{"derivedFrom":sQuery(id+"F0.wireOp",EDGE,"E62.sketch_text.stroke-0")}),-1.0]])]});
            var Q16;
            Q16=makeQuery(id+"F0.imprint","IMPRINT",FACE,{"disambiguationData":[TD([[makeQuery(id+"F0.imprint","IMPRINT",EDGE,{"derivedFrom":sQuery(id+"F0.wireOp",EDGE,"E66.sketch_text.stroke-0")}),-1.0]])]});
            var Q17;
            Q17=makeQuery(id+"F0.imprint","IMPRINT",FACE,{"disambiguationData":[TD([[makeQuery(id+"F0.imprint","IMPRINT",EDGE,{"derivedFrom":sQuery(id+"F0.wireOp",EDGE,"E66.sketch_text.stroke-6")}),-1.0]])]});
            var Q18;
            Q18=makeQuery(id+"F0.imprint","IMPRINT",FACE,{"disambiguationData":[TD([[makeQuery(id+"F0.imprint","IMPRINT",EDGE,{"derivedFrom":sQuery(id+"F0.wireOp",EDGE,"E66.sketch_text.stroke-18")}),-1.0]])]});
            var Q19;
            Q19=makeQuery(id+"F0.imprint","IMPRINT",FACE,{"disambiguationData":[TD([[makeQuery(id+"F0.imprint","IMPRINT",EDGE,{"derivedFrom":sQuery(id+"F0.wireOp",EDGE,"E66.sketch_text.stroke-42")}),-1.0]])]});
            var Q20;
            Q20=makeQuery(id+"F0.imprint","IMPRINT",FACE,{"disambiguationData":[TD([[makeQuery(id+"F0.imprint","IMPRINT",EDGE,{"derivedFrom":sQuery(id+"F0.wireOp",EDGE,"E65.sketch_text.stroke-42")}),-1.0]])]});
            var Q21;
            Q21=makeQuery(id+"F0.imprint","IMPRINT",FACE,{"disambiguationData":[TD([[makeQuery(id+"F0.imprint","IMPRINT",EDGE,{"derivedFrom":sQuery(id+"F0.wireOp",EDGE,"E65.sketch_text.stroke-18")}),-1.0]])]});
            var Q22;
            Q22=makeQuery(id+"F0.imprint","IMPRINT",FACE,{"disambiguationData":[TD([[makeQuery(id+"F0.imprint","IMPRINT",EDGE,{"derivedFrom":sQuery(id+"F0.wireOp",EDGE,"E65.sketch_text.stroke-6")}),-1.0]])]});
            var Q23;
            Q23=makeQuery(id+"F0.imprint","IMPRINT",FACE,{"disambiguationData":[TD([[makeQuery(id+"F0.imprint","IMPRINT",EDGE,{"derivedFrom":sQuery(id+"F0.wireOp",EDGE,"E65.sketch_text.stroke-0")}),-1.0]])]});
            var Q24;
            Q24=makeQuery(id+"F0.imprint","IMPRINT",FACE,{"disambiguationData":[TD([[makeQuery(id+"F0.imprint","IMPRINT",EDGE,{"derivedFrom":sQuery(id+"F0.wireOp",EDGE,"E63.sketch_text.stroke-42")}),-1.0]])]});
            var Q25;
            Q25=makeQuery(id+"F0.imprint","IMPRINT",FACE,{"disambiguationData":[TD([[makeQuery(id+"F0.imprint","IMPRINT",EDGE,{"derivedFrom":sQuery(id+"F0.wireOp",EDGE,"E63.sketch_text.stroke-18")}),-1.0]])]});
            var Q26;
            Q26=makeQuery(id+"F0.imprint","IMPRINT",FACE,{"disambiguationData":[TD([[makeQuery(id+"F0.imprint","IMPRINT",EDGE,{"derivedFrom":sQuery(id+"F0.wireOp",EDGE,"E63.sketch_text.stroke-6")}),-1.0]])]});
            var Q27;
            Q27=makeQuery(id+"F0.imprint","IMPRINT",FACE,{"disambiguationData":[TD([[makeQuery(id+"F0.imprint","IMPRINT",EDGE,{"derivedFrom":sQuery(id+"F0.wireOp",EDGE,"E63.sketch_text.stroke-0")}),-1.0]])]});
            var Q28;
            Q28=makeQuery(id+"F0.imprint","IMPRINT",FACE,{"disambiguationData":[TD([[makeQuery(id+"F0.imprint","IMPRINT",EDGE,{"derivedFrom":sQuery(id+"F0.wireOp",EDGE,"E64.sketch_text.stroke-6")}),-1.0]])]});
            var Q29;
            Q29=makeQuery(id+"F0.imprint","IMPRINT",FACE,{"disambiguationData":[TD([[makeQuery(id+"F0.imprint","IMPRINT",EDGE,{"derivedFrom":sQuery(id+"F0.wireOp",EDGE,"E64.sketch_text.stroke-0")}),-1.0]])]});
            var Q30;
            Q30=makeQuery(id+"F0.imprint","IMPRINT",FACE,{"disambiguationData":[TD([[makeQuery(id+"F0.imprint","IMPRINT",EDGE,{"derivedFrom":sQuery(id+"F0.wireOp",EDGE,"E64.sketch_text.stroke-18")}),-1.0]])]});
            var Q31;
            Q31=makeQuery(id+"F0.imprint","IMPRINT",FACE,{"disambiguationData":[TD([[makeQuery(id+"F0.imprint","IMPRINT",EDGE,{"derivedFrom":sQuery(id+"F0.wireOp",EDGE,"E64.sketch_text.stroke-42")}),-1.0]])]});
            extrude(context, id + "F10", {"entities" : qUnion([Q0, Q1, Q2, Q3, Q4, Q5, Q6, Q7, Q8, Q9, Q10, Q11, Q12, Q13, Q14, Q15, Q16, Q17, Q18, Q19, Q20, Q21, Q22, Q23, Q24, Q25, Q26, Q27, Q28, Q29, Q30, Q31]), "oppositeDirection" : true, "depth" : 1.6 * mm});
        }
    });
